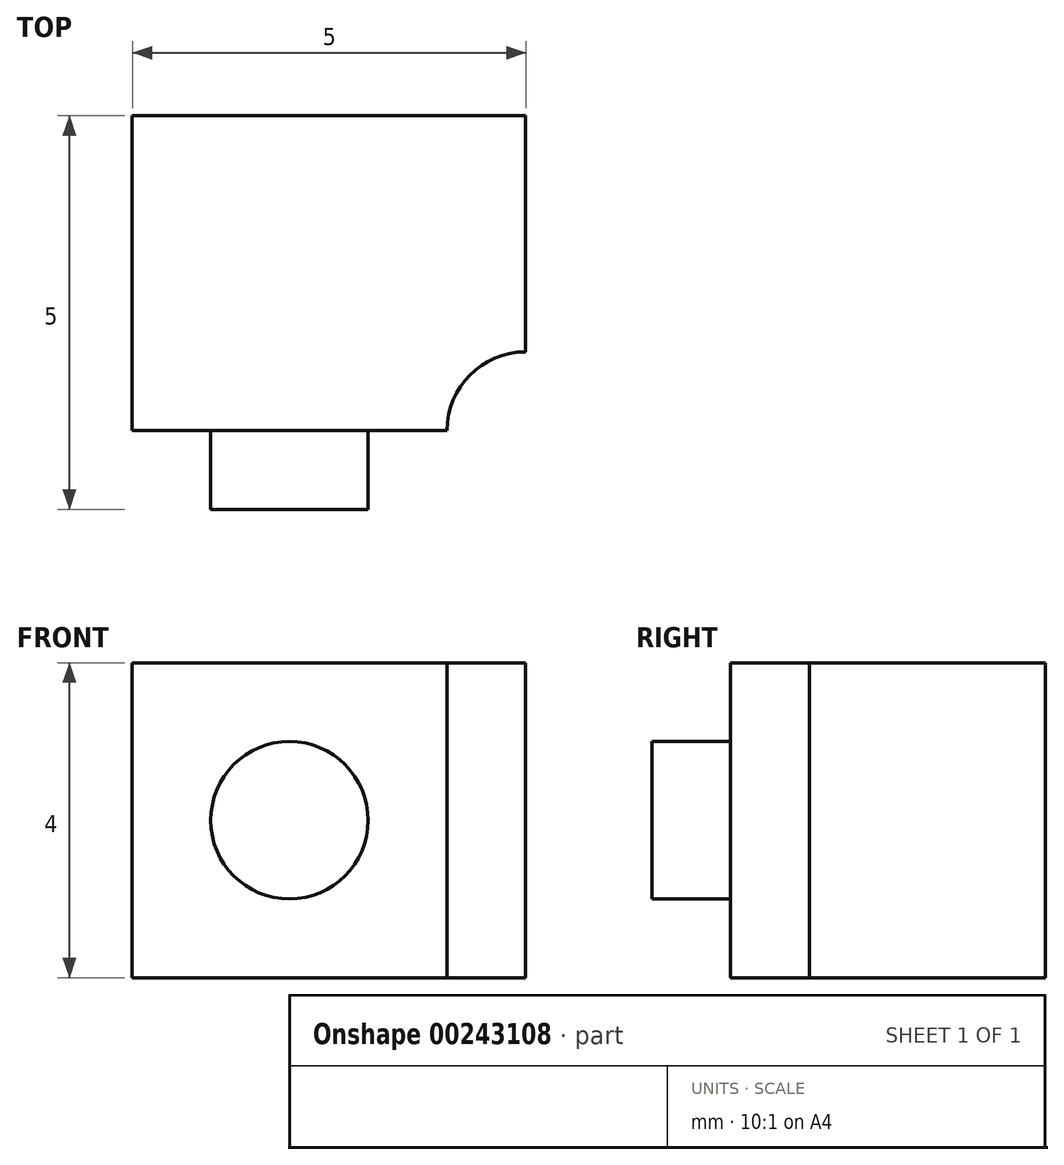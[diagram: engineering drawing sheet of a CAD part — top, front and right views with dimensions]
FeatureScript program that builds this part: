
annotation { "Feature Type Name" : "Feature", "Feature Type Description" : "" }
export const myFeature = defineFeature(function(context is Context, id is Id, definition is map)
    precondition{}
    {
        {
            var Q0;
            Q0=qCreatedBy(makeId("Top.planeOp"),FACE);
            var sketch = newSketch(context, id + "F0", { "sketchPlane" : qUnion([Q0])});
            skLineSegment(sketch, "E0.bottom", {"start": v(19.34, 17.66) * mm, "end": v(24.34, 17.66) * mm});
            skLineSegment(sketch, "E0.top", {"start": v(19.34, 13.66) * mm, "end": v(24.34, 13.66) * mm});
            skLineSegment(sketch, "E0.left", {"start": v(19.34, 17.66) * mm, "end": v(19.34, 13.66) * mm});
            skLineSegment(sketch, "E0.right", {"start": v(24.34, 17.66) * mm, "end": v(24.34, 13.66) * mm});
            skSolve(sketch);
        }
        {
            var Q0;
            Q0 = qSketchRegion(id + "F0", true);
            extrude(context, id + "F1", {"entities" : qUnion([Q0]), "depth" : 4 * mm});
        }
        {
            var Q0;
            Q0=makeQuery(id+"F1.opExtrude","CAP_FACE",FACE,{"disambiguationData":[OSD([sQuery(id+"F0.wireOp",EDGE,"E0.bottom"),sQuery(id+"F0.wireOp",EDGE,"E0.top"),sQuery(id+"F0.wireOp",EDGE,"E0.left"),sQuery(id+"F0.wireOp",EDGE,"E0.right")])],"isStart":false});
            var sketch = newSketch(context, id + "F2", { "sketchPlane" : qUnion([Q0])});
            skCircle(sketch, "E1", {"center": v(24.34, 13.66) * mm, "radius": 1 * mm});
            skSolve(sketch);
        }
        {
            var Q0;
            Q0 = qSketchRegion(id + "F2", true);
            extrude(context, id + "F3", {"entities" : qUnion([Q0]), "operationType" : NewBodyOperationType.REMOVE, "oppositeDirection" : true, "depth" : 4.1 * mm});
        }
        {
            var Q0;
            Q0=makeQuery(id+"F1.opExtrude","SWEPT_FACE",FACE,{"disambiguationData":[OSD([sQuery(id+"F0.wireOp",EDGE,"E0.top")])]});
            var sketch = newSketch(context, id + "F4", { "sketchPlane" : qUnion([Q0])});
            skCircle(sketch, "E2", {"center": v(21.34, 2) * mm, "radius": 1 * mm});
            skSolve(sketch);
        }
        {
            var Q0;
            Q0 = qSketchRegion(id + "F4", true);
            extrude(context, id + "F5", {"entities" : qUnion([Q0]), "operationType" : NewBodyOperationType.ADD, "depth" : 1 * mm});
        }
    });
